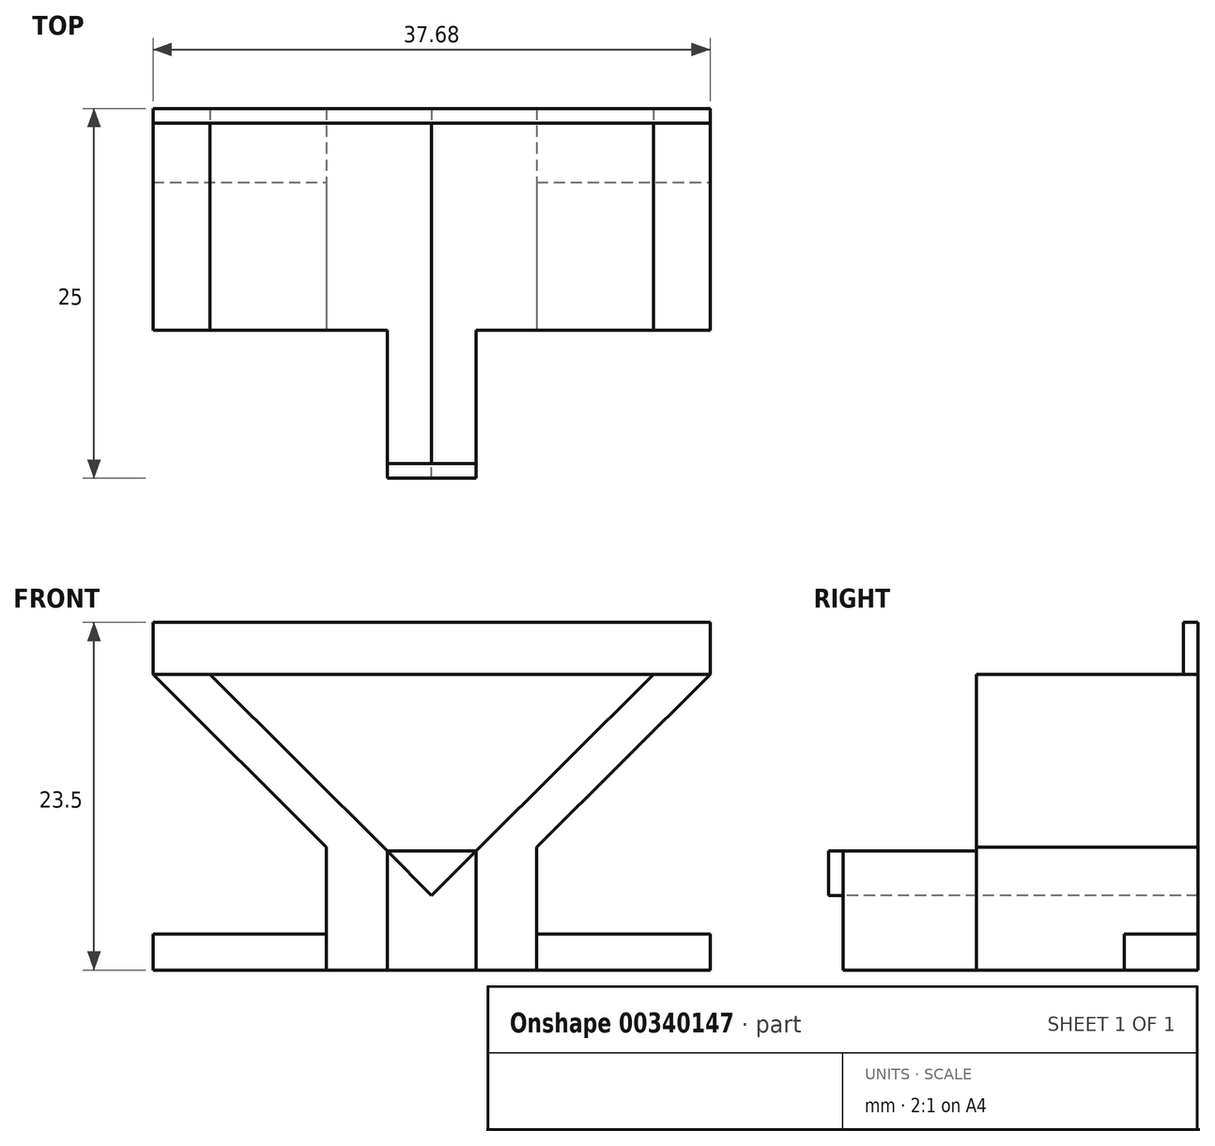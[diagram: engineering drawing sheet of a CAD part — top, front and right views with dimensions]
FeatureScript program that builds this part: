
annotation { "Feature Type Name" : "Feature", "Feature Type Description" : "" }
export const myFeature = defineFeature(function(context is Context, id is Id, definition is map)
    precondition{}
    {
        {
            var Q0;
            Q0=qCreatedBy(makeId("Front.planeOp"),FACE);
            var sketch = newSketch(context, id + "F0", { "sketchPlane" : qUnion([Q0])});
            skLineSegment(sketch, "E0.bottom", {"start": v(0, 0) * mm, "end": v(60, 0) * mm});
            skLineSegment(sketch, "E0.left", {"start": v(0, 0) * mm, "end": v(0, 20) * mm});
            skLineSegment(sketch, "E0.right", {"start": v(60, 0) * mm, "end": v(60, 20) * mm});
            skLineSegment(sketch, "E1", {"start": v(15, 20) * mm, "end": v(0, 20) * mm});
            skLineSegment(sketch, "E2", {"start": v(45, 20) * mm, "end": v(60, 20) * mm});
            skLineSegment(sketch, "E3", {"start": v(15, 20) * mm, "end": v(30, 5.04) * mm});
            skLineSegment(sketch, "E4", {"start": v(30, 5.04) * mm, "end": v(45, 20) * mm});
            skSolve(sketch);
        }
        {
            var Q0;
            Q0=makeQuery(id+"F0.imprint","IMPRINT",FACE,{"disambiguationData":[TD([[makeQuery(id+"F0.imprint","IMPRINT",EDGE,{"derivedFrom":sQuery(id+"F0.wireOp",EDGE,"E0.bottom")}),1.0]])]});
            extrude(context, id + "F1", {"entities" : qUnion([Q0]), "oppositeDirection" : true, "depth" : 15 * mm});
        }
        {
            var Q0;
            Q0=makeQuery(id+"F1.opExtrude","CAP_FACE",FACE,{"disambiguationData":[OSD([sQuery(id+"F0.wireOp",EDGE,"E0.bottom"),sQuery(id+"F0.wireOp",EDGE,"E0.left"),sQuery(id+"F0.wireOp",EDGE,"E0.right"),sQuery(id+"F0.wireOp",EDGE,"E1"),sQuery(id+"F0.wireOp",EDGE,"E2"),sQuery(id+"F0.wireOp",EDGE,"E3"),sQuery(id+"F0.wireOp",EDGE,"E4")])],"isStart":true});
            var sketch = newSketch(context, id + "F2", { "sketchPlane" : qUnion([Q0])});
            skPoint(sketch, "E5.startSnap0", {"position": v(0, 10) * mm});
            skPoint(sketch, "E5.startSnap1", {"position": v(22.5, 12.52) * mm});
            skLineSegment(sketch, "E6.MirrorCS", {"start": v(41.34, 2.42) * mm, "end": v(60, 2.42) * mm});
            skLineSegment(sketch, "E7", {"start": v(18.66, 12.52) * mm, "end": v(14.4, 16.77) * mm});
            skLineSegment(sketch, "E8", {"start": v(14.4, 16.77) * mm, "end": v(11.16, 20) * mm});
            skLineSegment(sketch, "E9", {"start": v(30, 5.04) * mm, "end": v(30, 0) * mm});
            skLineSegment(sketch, "E10.MirrorCS", {"start": v(45.6, 16.77) * mm, "end": v(48.84, 20) * mm});
            skLineSegment(sketch, "E11.MirrorCS", {"start": v(41.34, 12.52) * mm, "end": v(45.6, 16.77) * mm});
            skLineSegment(sketch, "E12", {"start": v(18.66, 12.52) * mm, "end": v(27.12, 4.08) * mm});
            skLineSegment(sketch, "E13.MirrorCS", {"start": v(41.34, 12.52) * mm, "end": v(32.88, 4.08) * mm});
            skLineSegment(sketch, "E14.MirrorCS", {"start": v(18.66, 2.42) * mm, "end": v(0, 2.42) * mm});
            skLineSegment(sketch, "E15", {"start": v(18.66, 2.42) * mm, "end": v(27.12, 2.42) * mm});
            skLineSegment(sketch, "E16", {"start": v(27.12, 2.42) * mm, "end": v(27.12, 4.08) * mm});
            skLineSegment(sketch, "E17", {"start": v(32.88, 4.08) * mm, "end": v(32.88, 2.42) * mm});
            skLineSegment(sketch, "E18", {"start": v(32.88, 2.42) * mm, "end": v(41.34, 2.42) * mm});
            skLineSegment(sketch, "E19", {"start": v(22.89, 8.3) * mm, "end": v(22.89, 2.42) * mm});
            skLineSegment(sketch, "E20", {"start": v(37.11, 2.42) * mm, "end": v(37.11, 8.3) * mm});
            skLineSegment(sketch, "E21", {"start": v(27.12, 2.42) * mm, "end": v(32.88, 2.42) * mm});
            skLineSegment(sketch, "E22", {"start": v(22.89, 2.42) * mm, "end": v(22.89, 0) * mm});
            skLineSegment(sketch, "E23", {"start": v(37.11, 2.42) * mm, "end": v(37.11, 0) * mm});
            skLineSegment(sketch, "E24.bottom", {"start": v(11.16, 20) * mm, "end": v(15, 20) * mm});
            skLineSegment(sketch, "E24.top", {"start": v(11.16, 23.5) * mm, "end": v(15, 23.5) * mm});
            skLineSegment(sketch, "E24.left", {"start": v(11.16, 20) * mm, "end": v(11.16, 23.5) * mm});
            skLineSegment(sketch, "E25.bottom", {"start": v(15, 23.5) * mm, "end": v(48.84, 23.5) * mm});
            skLineSegment(sketch, "E25.top", {"start": v(15, 20) * mm, "end": v(48.84, 20) * mm});
            skLineSegment(sketch, "E25.right", {"start": v(48.84, 23.5) * mm, "end": v(48.84, 20) * mm});
            skSolve(sketch);
        }
        {
            var Q0;
            {var subQ6=sQuery(id+"F2.wireOp",EDGE,"E7");Q0=makeQuery(id+"F2.imprint","IMPRINT",FACE,{"disambiguationData":[TD([[makeQuery(id+"F2.imprint","IMPRINT",EDGE,{"derivedFrom":subQ6}),1.0]])]});}
            var Q1;
            {var subQ7=sQuery(id+"F2.wireOp",EDGE,"E6.MirrorCS");Q1=makeQuery(id+"F2.imprint","IMPRINT",FACE,{"disambiguationData":[TD([[makeQuery(id+"F2.imprint","IMPRINT",EDGE,{"derivedFrom":subQ7}),1.0]])]});}
            extrude(context, id + "F3", {"entities" : qUnion([Q0, Q1]), "operationType" : NewBodyOperationType.REMOVE, "endBound" : BoundingType.UP_TO_NEXT, "oppositeDirection" : true, "depth" : 25 * mm});
        }
        {
            var Q0;
            {var subQ1=sQuery(id+"F2.wireOp",EDGE,"E14.MirrorCS");Q0=makeQuery(id+"F2.imprint","IMPRINT",FACE,{"disambiguationData":[TD([[makeQuery(id+"F2.imprint","IMPRINT",EDGE,{"derivedFrom":subQ1}),1.0]])]});}
            var Q1;
            {var subQ5=sQuery(id+"F2.wireOp",EDGE,"E6.MirrorCS");Q1=makeQuery(id+"F2.imprint","IMPRINT",FACE,{"disambiguationData":[TD([[makeQuery(id+"F2.imprint","IMPRINT",EDGE,{"derivedFrom":subQ5}),-1.0]])]});}
            extrude(context, id + "F4", {"entities" : qUnion([Q0, Q1]), "operationType" : NewBodyOperationType.REMOVE, "oppositeDirection" : true, "depth" : 10 * mm});
        }
        {
            var Q0;
            {var subQ0=sQuery(id+"F2.wireOp",EDGE,"E24.bottom");Q0=makeQuery(id+"F2.imprint","IMPRINT",FACE,{"disambiguationData":[TD([[makeQuery(id+"F2.imprint","IMPRINT",EDGE,{"derivedFrom":subQ0}),-1.0]])]});}
            var Q1;
            Q1=makeQuery(id+"F1.opExtrude","CAP_FACE",FACE,{"disambiguationData":[OSD([sQuery(id+"F0.wireOp",EDGE,"E0.bottom"),sQuery(id+"F0.wireOp",EDGE,"E0.left"),sQuery(id+"F0.wireOp",EDGE,"E0.right"),sQuery(id+"F0.wireOp",EDGE,"E1"),sQuery(id+"F0.wireOp",EDGE,"E2"),sQuery(id+"F0.wireOp",EDGE,"E3"),sQuery(id+"F0.wireOp",EDGE,"E4")])],"isStart":false});
            extrude(context, id + "F5", {"entities" : qUnion([Q0]), "operationType" : NewBodyOperationType.ADD, "endBound" : BoundingType.UP_TO_SURFACE, "oppositeDirection" : true, "endBoundEntityFace" : qUnion([Q1]), "depth" : 18.9 * mm});
        }
        {
            var Q0;
            {var subQ0=sQuery(id+"F2.wireOp",EDGE,"E24.bottom");Q0=makeQuery(id+"F2.imprint","IMPRINT",FACE,{"disambiguationData":[TD([[makeQuery(id+"F2.imprint","IMPRINT",EDGE,{"derivedFrom":subQ0}),-1.0]])]});}
            extrude(context, id + "F6", {"entities" : qUnion([Q0]), "operationType" : NewBodyOperationType.REMOVE, "oppositeDirection" : true, "depth" : 14 * mm});
        }
        {
            var Q0;
            Q0=makeQuery(id+"F5.boolean.opBoolean","MERGE",FACE,{"derivedFrom":[makeQuery(id+"F1.opExtrude","CAP_FACE",FACE,{"disambiguationData":[OSD([sQuery(id+"F0.wireOp",EDGE,"E0.bottom"),sQuery(id+"F0.wireOp",EDGE,"E0.left"),sQuery(id+"F0.wireOp",EDGE,"E0.right"),sQuery(id+"F0.wireOp",EDGE,"E1"),sQuery(id+"F0.wireOp",EDGE,"E2"),sQuery(id+"F0.wireOp",EDGE,"E3"),sQuery(id+"F0.wireOp",EDGE,"E4")])],"isStart":true}),makeQuery(id+"F5.opExtrude","CAP_FACE",FACE,{"disambiguationData":[OSD([sQuery(id+"F2.wireOp",EDGE,"E24.bottom"),sQuery(id+"F2.wireOp",EDGE,"E24.top"),sQuery(id+"F2.wireOp",EDGE,"E24.left"),sQuery(id+"F2.wireOp",EDGE,"E25.bottom"),sQuery(id+"F2.wireOp",EDGE,"E25.top"),sQuery(id+"F2.wireOp",EDGE,"E25.right")])],"isStart":true})]});
            var sketch = newSketch(context, id + "F7", { "sketchPlane" : qUnion([Q0])});
            skLineSegment(sketch, "E26", {"start": v(29, 0) * mm, "end": v(31, 0) * mm});
            skLineSegment(sketch, "E27", {"start": v(27, 6.03) * mm, "end": v(27, 8.04) * mm});
            skLineSegment(sketch, "E28", {"start": v(27, 8.04) * mm, "end": v(27, 0) * mm});
            skLineSegment(sketch, "E29", {"start": v(33.02, 5.04) * mm, "end": v(33.02, 8.05) * mm});
            skLineSegment(sketch, "E30", {"start": v(33.02, 8.05) * mm, "end": v(33.02, 0) * mm});
            skSolve(sketch);
        }
        {
            var Q0;
            {var subQ11=sQuery(id+"F7.wireOp",EDGE,"E26");Q0=makeQuery(id+"F7.imprint","IMPRINT",FACE,{"disambiguationData":[TD([[makeQuery(id+"F7.imprint","IMPRINT",EDGE,{"derivedFrom":subQ11}),1.0]])]});}
            extrude(context, id + "F8", {"entities" : qUnion([Q0]), "operationType" : NewBodyOperationType.ADD, "depth" : 9 * mm});
        }
        {
            var Q0;
            Q0=makeQuery(id+"F1.opExtrude","SWEPT_FACE",FACE,{"disambiguationData":[OSD([sQuery(id+"F0.wireOp",EDGE,"E0.left")])]});
            var Q1;
            Q1=makeQuery(id+"F5.opExtrude","SWEPT_FACE",FACE,{"disambiguationData":[OSD([sQuery(id+"F2.wireOp",EDGE,"E24.left")])]});
            extrude(context, id + "F9", {"entities" : qUnion([Q0]), "operationType" : NewBodyOperationType.REMOVE, "endBound" : BoundingType.UP_TO_SURFACE, "oppositeDirection" : true, "endBoundEntityFace" : qUnion([Q1]), "depth" : 25 * mm});
        }
        {
            var Q0;
            Q0=makeQuery(id+"F1.opExtrude","SWEPT_FACE",FACE,{"disambiguationData":[OSD([sQuery(id+"F0.wireOp",EDGE,"E0.right")])]});
            var Q1;
            Q1=makeQuery(id+"F5.opExtrude","SWEPT_FACE",FACE,{"disambiguationData":[OSD([sQuery(id+"F2.wireOp",EDGE,"E25.right")])]});
            extrude(context, id + "F10", {"entities" : qUnion([Q0]), "operationType" : NewBodyOperationType.REMOVE, "endBound" : BoundingType.UP_TO_SURFACE, "oppositeDirection" : true, "endBoundEntityFace" : qUnion([Q1]), "depth" : 25 * mm});
        }
        {
            var Q0;
            Q0=makeQuery(id+"F8.opExtrude","CAP_FACE",FACE,{"disambiguationData":[OSD([sQuery(id+"F0.wireOp",EDGE,"E0.bottom"),sQuery(id+"F0.wireOp",EDGE,"E3"),sQuery(id+"F0.wireOp",EDGE,"E4"),sQuery(id+"F7.wireOp",EDGE,"E26"),sQuery(id+"F7.wireOp",EDGE,"E28"),sQuery(id+"F7.wireOp",EDGE,"E30")])],"isStart":false});
            var sketch = newSketch(context, id + "F11", { "sketchPlane" : qUnion([Q0])});
            skLineSegment(sketch, "E31", {"start": v(27, 8.04) * mm, "end": v(33.02, 8.05) * mm});
            skSolve(sketch);
        }
        {
            var Q0;
            Q0=makeQuery(id+"F11.imprint","IMPRINT",FACE,{"disambiguationData":[TD([[makeQuery(id+"F11.imprint","IMPRINT",EDGE,{"derivedFrom":sQuery(id+"F11.wireOp",EDGE,"E31")}),-1.0]])]});
            var Q1;
            Q1=makeQuery(id+"F11.imprint","IMPRINT",FACE,{"disambiguationData":[TD([[makeQuery(id+"F11.imprint","IMPRINT",EDGE,{"derivedFrom":makeQuery(id+"F8.opExtrude","CAP_EDGE",EDGE,{"disambiguationData":[OSD([sQuery(id+"F7.wireOp",EDGE,"E28")])],"isStart":false})}),1.0]])]});
            extrude(context, id + "F12", {"entities" : qUnion([Q0, Q1]), "operationType" : NewBodyOperationType.ADD, "depth" : 1 * mm});
        }
    });
